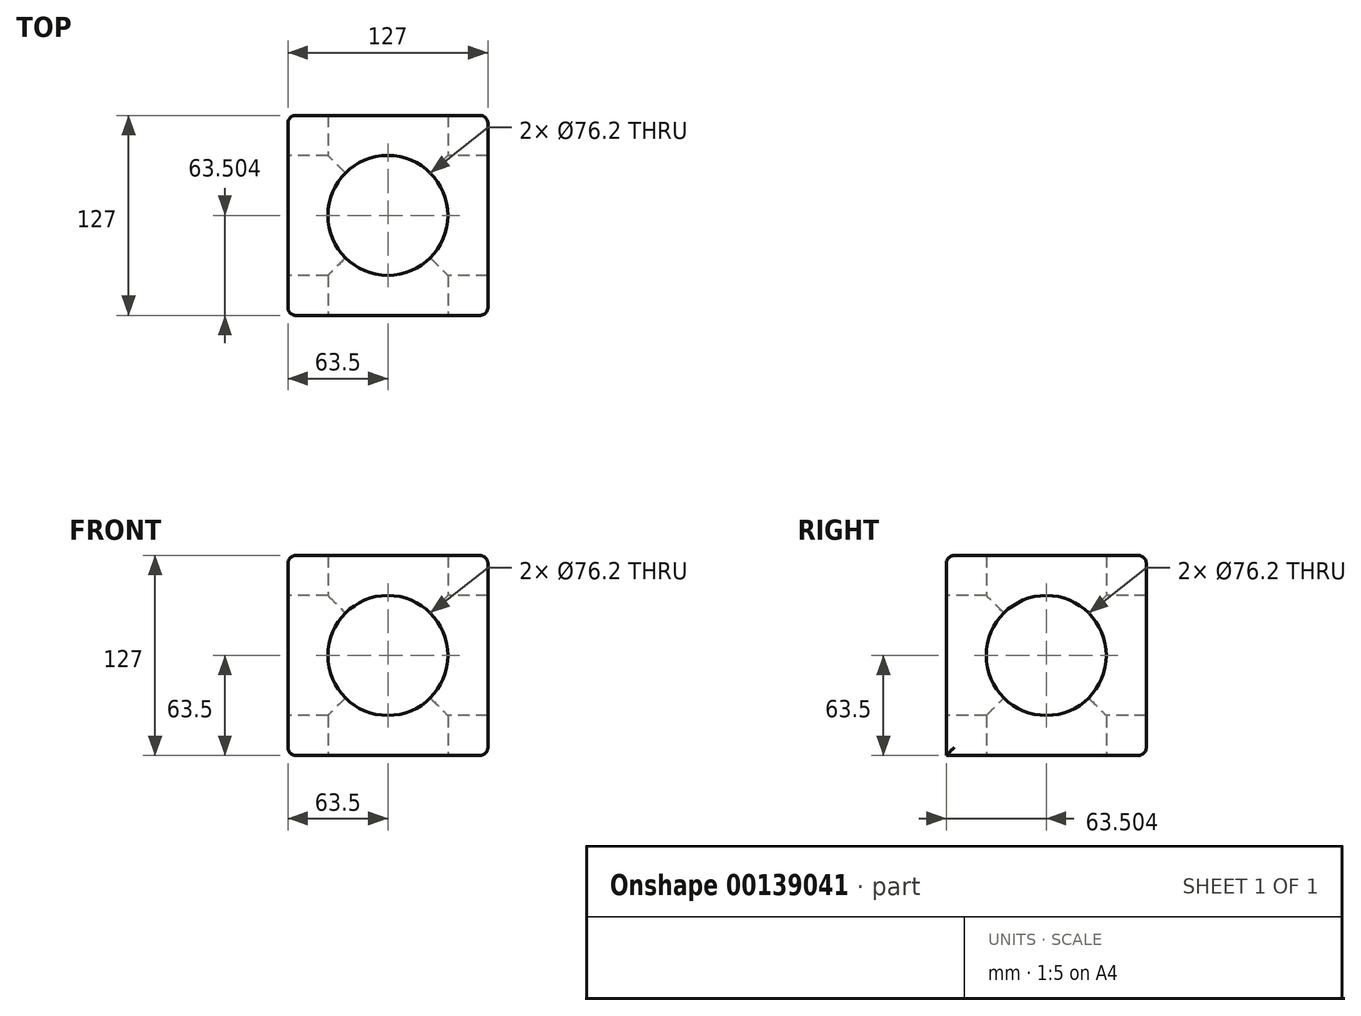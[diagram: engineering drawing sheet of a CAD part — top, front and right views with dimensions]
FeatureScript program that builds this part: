
annotation { "Feature Type Name" : "Feature", "Feature Type Description" : "" }
export const myFeature = defineFeature(function(context is Context, id is Id, definition is map)
    precondition{}
    {
        {
            var Q0;
            Q0=qCreatedBy(makeId("Top.planeOp"),FACE);
            var sketch = newSketch(context, id + "F0", { "sketchPlane" : qUnion([Q0])});
            skLineSegment(sketch, "E0.bottom", {"start": v(-57.54, 57.63) * mm, "end": v(69.46, 57.63) * mm});
            skLineSegment(sketch, "E0.top", {"start": v(-57.54, -69.37) * mm, "end": v(69.46, -69.37) * mm});
            skLineSegment(sketch, "E0.left", {"start": v(-57.54, 57.63) * mm, "end": v(-57.54, -69.37) * mm});
            skLineSegment(sketch, "E0.right", {"start": v(69.46, 57.63) * mm, "end": v(69.46, -69.37) * mm});
            skSolve(sketch);
        }
        {
            var Q0;
            Q0 = qSketchRegion(id + "F0", true);
            extrude(context, id + "F1", {"entities" : qUnion([Q0]), "depth" : 127 * mm});
        }
        {
            var Q0;
            Q0=makeQuery(id+"F1.opExtrude","SWEPT_FACE",FACE,{"disambiguationData":[OSD([sQuery(id+"F0.wireOp",EDGE,"E0.left")])]});
            var sketch = newSketch(context, id + "F2", { "sketchPlane" : qUnion([Q0])});
            skLineSegment(sketch, "E1", {"start": v(-57.63, 127) * mm, "end": v(69.37, 0) * mm, "construction": true});
            skCircle(sketch, "E2", {"center": v(5.87, 63.5) * mm, "radius": 38.1 * mm});
            skSolve(sketch);
        }
        {
            var Q0;
            Q0 = qSketchRegion(id + "F2", true);
            extrude(context, id + "F3", {"entities" : qUnion([Q0]), "operationType" : NewBodyOperationType.REMOVE, "oppositeDirection" : true, "depth" : 127 * mm});
        }
        {
            var Q0;
            Q0=makeQuery(id+"F1.opExtrude","SWEPT_FACE",FACE,{"disambiguationData":[OSD([sQuery(id+"F0.wireOp",EDGE,"E0.top")])]});
            var sketch = newSketch(context, id + "F4", { "sketchPlane" : qUnion([Q0])});
            skLineSegment(sketch, "E3", {"start": v(-57.54, 127) * mm, "end": v(69.46, 0) * mm, "construction": true});
            skCircle(sketch, "E4", {"center": v(5.96, 63.5) * mm, "radius": 38.1 * mm});
            skSolve(sketch);
        }
        {
            var Q0;
            Q0 = qSketchRegion(id + "F4", true);
            extrude(context, id + "F5", {"entities" : qUnion([Q0]), "operationType" : NewBodyOperationType.REMOVE, "oppositeDirection" : true, "depth" : 127 * mm});
        }
        {
            var Q0;
            Q0=makeQuery(id+"F1.opExtrude","CAP_FACE",FACE,{"disambiguationData":[OSD([sQuery(id+"F0.wireOp",EDGE,"E0.bottom"),sQuery(id+"F0.wireOp",EDGE,"E0.top"),sQuery(id+"F0.wireOp",EDGE,"E0.left"),sQuery(id+"F0.wireOp",EDGE,"E0.right")])],"isStart":true});
            var sketch = newSketch(context, id + "F6", { "sketchPlane" : qUnion([Q0])});
            skLineSegment(sketch, "E5", {"start": v(-57.54, 69.37) * mm, "end": v(69.46, -57.63) * mm, "construction": true});
            skCircle(sketch, "E6", {"center": v(5.96, 5.87) * mm, "radius": 38.1 * mm});
            skSolve(sketch);
        }
        {
            var Q0;
            Q0 = qSketchRegion(id + "F6", true);
            extrude(context, id + "F7", {"entities" : qUnion([Q0]), "operationType" : NewBodyOperationType.REMOVE, "oppositeDirection" : true, "depth" : 127 * mm});
        }
        {
            var Q0;
            Q0=makeQuery(id+"F1.opExtrude","SWEPT_EDGE",EDGE,{"disambiguationData":[OSD([sQuery(id+"F0.wireOp",EDGE,"E0.bottom"),sQuery(id+"F0.wireOp",EDGE,"E0.left")])]});
            var Q1;
            Q1=makeQuery(id+"F1.opExtrude","CAP_EDGE",EDGE,{"disambiguationData":[OSD([sQuery(id+"F0.wireOp",EDGE,"E0.bottom")])],"isStart":true});
            var Q2;
            Q2=makeQuery(id+"F1.opExtrude","SWEPT_EDGE",EDGE,{"disambiguationData":[OSD([sQuery(id+"F0.wireOp",EDGE,"E0.bottom"),sQuery(id+"F0.wireOp",EDGE,"E0.right")])]});
            var Q3;
            Q3=makeQuery(id+"F1.opExtrude","CAP_EDGE",EDGE,{"disambiguationData":[OSD([sQuery(id+"F0.wireOp",EDGE,"E0.bottom")])],"isStart":false});
            var Q4;
            Q4=makeQuery(id+"F1.opExtrude","CAP_EDGE",EDGE,{"disambiguationData":[OSD([sQuery(id+"F0.wireOp",EDGE,"E0.left")])],"isStart":true});
            var Q5;
            Q5=makeQuery(id+"F1.opExtrude","SWEPT_EDGE",EDGE,{"disambiguationData":[OSD([sQuery(id+"F0.wireOp",EDGE,"E0.top"),sQuery(id+"F0.wireOp",EDGE,"E0.left")])]});
            var Q6;
            Q6=makeQuery(id+"F1.opExtrude","CAP_EDGE",EDGE,{"disambiguationData":[OSD([sQuery(id+"F0.wireOp",EDGE,"E0.left")])],"isStart":false});
            var Q7;
            Q7=makeQuery(id+"F1.opExtrude","CAP_EDGE",EDGE,{"disambiguationData":[OSD([sQuery(id+"F0.wireOp",EDGE,"E0.top")])],"isStart":false});
            var Q8;
            Q8=makeQuery(id+"F1.opExtrude","CAP_EDGE",EDGE,{"disambiguationData":[OSD([sQuery(id+"F0.wireOp",EDGE,"E0.right")])],"isStart":false});
            var Q9;
            Q9=makeQuery(id+"F1.opExtrude","CAP_EDGE",EDGE,{"disambiguationData":[OSD([sQuery(id+"F0.wireOp",EDGE,"E0.right")])],"isStart":true});
            var Q10;
            Q10=makeQuery(id+"F1.opExtrude","SWEPT_EDGE",EDGE,{"disambiguationData":[OSD([sQuery(id+"F0.wireOp",EDGE,"E0.top"),sQuery(id+"F0.wireOp",EDGE,"E0.right")])]});
            var Q11;
            Q11=makeQuery(id+"F3.boolean.opBoolean","COPY",EDGE,{"derivedFrom":makeQuery(id+"F3.opExtrude","CAP_EDGE",EDGE,{"disambiguationData":[OSD([sQuery(id+"F2.wireOp",EDGE,"E2")])],"isStart":false})});
            var Q12;
            Q12=makeQuery(id+"F7.boolean.opBoolean","COPY",EDGE,{"derivedFrom":makeQuery(id+"F7.opExtrude","CAP_EDGE",EDGE,{"disambiguationData":[OSD([sQuery(id+"F6.wireOp",EDGE,"E6")])],"isStart":true})});
            var Q13;
            Q13=makeQuery(id+"F3.boolean.opBoolean","COPY",EDGE,{"derivedFrom":makeQuery(id+"F3.opExtrude","CAP_EDGE",EDGE,{"disambiguationData":[OSD([sQuery(id+"F2.wireOp",EDGE,"E2")])],"isStart":true})});
            var Q14;
            Q14=makeQuery(id+"F5.boolean.opBoolean","COPY",EDGE,{"derivedFrom":makeQuery(id+"F5.opExtrude","CAP_EDGE",EDGE,{"disambiguationData":[OSD([sQuery(id+"F4.wireOp",EDGE,"E4")])],"isStart":true})});
            fillet(context, id + "F8", {"entities" : qUnion([Q0, Q1, Q2, Q3, Q4, Q5, Q6, Q7, Q8, Q9, Q10, Q11, Q12, Q13, Q14]), "radius" : 5.08 * mm, "tangentPropagation" : true, "allowEdgeOverflow" : false});
        }
    });
